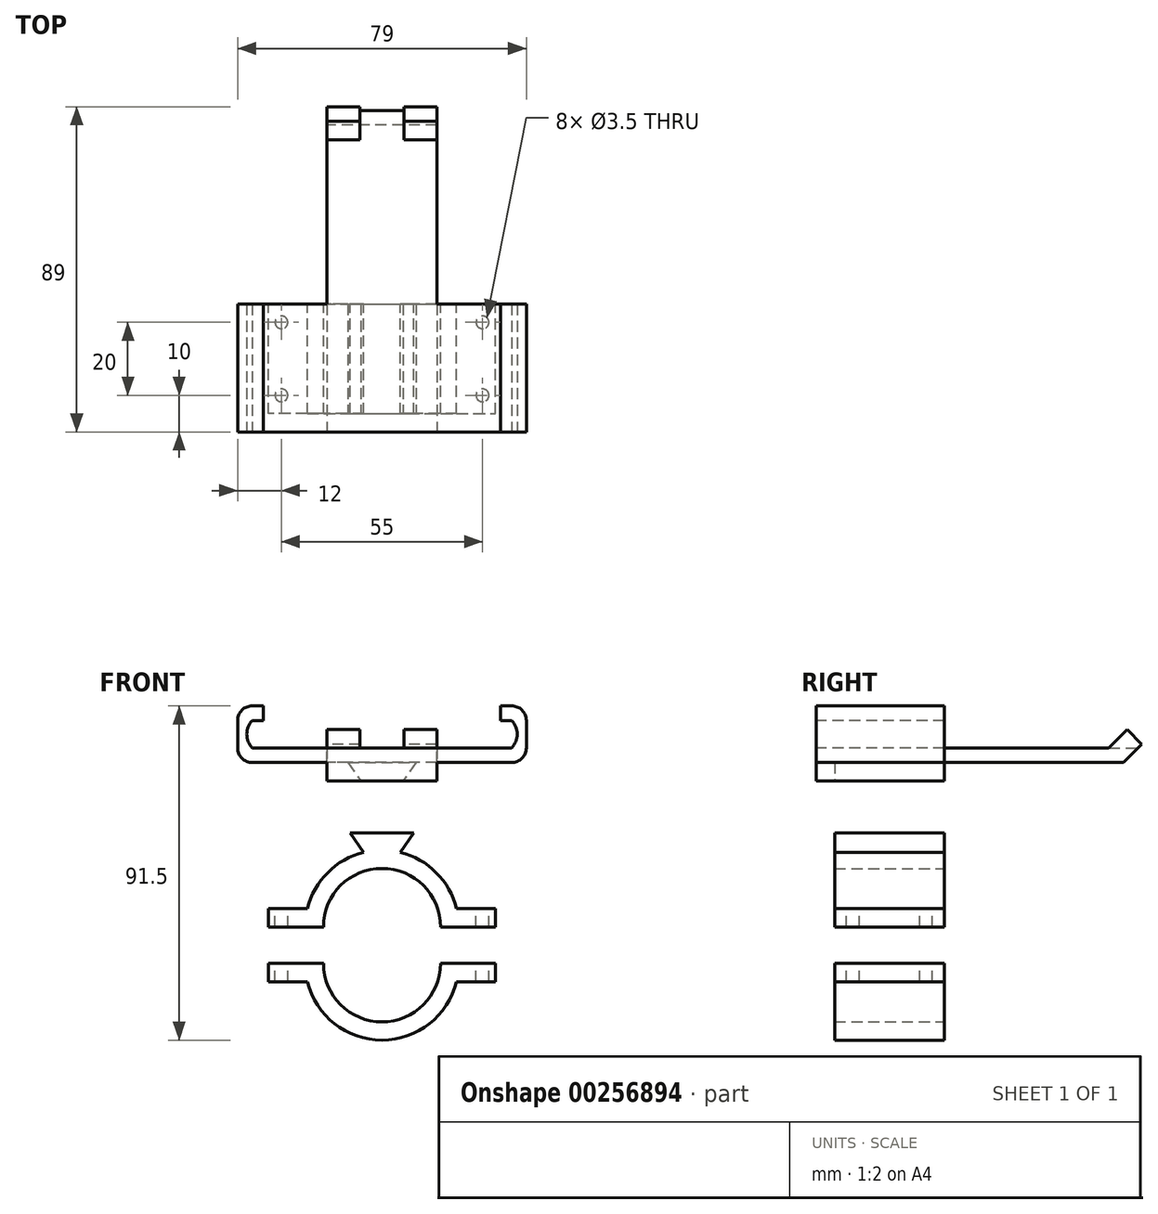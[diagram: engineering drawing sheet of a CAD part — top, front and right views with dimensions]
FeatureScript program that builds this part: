
annotation { "Feature Type Name" : "Feature", "Feature Type Description" : "" }
export const myFeature = defineFeature(function(context is Context, id is Id, definition is map)
    precondition{}
    {
        {
            var Q0;
            Q0=qCreatedBy(makeId("Front.planeOp"),FACE);
            var sketch = newSketch(context, id + "F0", { "sketchPlane" : qUnion([Q0])});
            skArc(sketch, "E0", {"start": v(16, 0) * mm, "mid": v(0, 16) * mm, "end": v(-16, 0) * mm});
            skArc(sketch, "E1", {"start": v(21, 0) * mm, "mid": v(0, 21) * mm, "end": v(-21, 0) * mm});
            skLineSegment(sketch, "E2", {"start": v(16, 0) * mm, "end": v(-16, 0) * mm, "construction": true});
            skLineSegment(sketch, "E3", {"start": v(21, 0) * mm, "end": v(16, 0) * mm});
            skLineSegment(sketch, "E4", {"start": v(-16, 0) * mm, "end": v(-21, 0) * mm});
            skLineSegment(sketch, "E5.bottom", {"start": v(16, 0) * mm, "end": v(31, 0) * mm});
            skLineSegment(sketch, "E5.top", {"start": v(16, 5) * mm, "end": v(31, 5) * mm});
            skLineSegment(sketch, "E5.left", {"start": v(16, 0) * mm, "end": v(16, 5) * mm});
            skLineSegment(sketch, "E5.right", {"start": v(31, 0) * mm, "end": v(31, 5) * mm});
            skLineSegment(sketch, "E6.bottom", {"start": v(-16, 0) * mm, "end": v(-31, 0) * mm});
            skLineSegment(sketch, "E6.top", {"start": v(-16, 5) * mm, "end": v(-31, 5) * mm});
            skLineSegment(sketch, "E6.left", {"start": v(-16, 0) * mm, "end": v(-16, 5) * mm});
            skLineSegment(sketch, "E6.right", {"start": v(-31, 0) * mm, "end": v(-31, 5) * mm});
            skLineSegment(sketch, "E7", {"start": v(-16, -10) * mm, "end": v(16, -10) * mm, "construction": true});
            skArc(sketch, "E8", {"start": v(-16, -10) * mm, "mid": v(0, -26) * mm, "end": v(16, -10) * mm});
            skLineSegment(sketch, "E9", {"start": v(16, -10) * mm, "end": v(21, -10) * mm});
            skLineSegment(sketch, "E10", {"start": v(-16, -10) * mm, "end": v(-21, -10) * mm});
            skArc(sketch, "E11", {"start": v(-21, -10) * mm, "mid": v(0, -31) * mm, "end": v(21, -10) * mm});
            skLineSegment(sketch, "E12.bottom", {"start": v(16, -10) * mm, "end": v(31, -10) * mm});
            skLineSegment(sketch, "E12.top", {"start": v(16, -15) * mm, "end": v(31, -15) * mm});
            skLineSegment(sketch, "E12.left", {"start": v(16, -10) * mm, "end": v(16, -15) * mm});
            skLineSegment(sketch, "E12.right", {"start": v(31, -10) * mm, "end": v(31, -15) * mm});
            skPoint(sketch, "E13.oppositeSnap0", {"position": v(23.5, -15) * mm});
            skLineSegment(sketch, "E13.bottom", {"start": v(-16, -10) * mm, "end": v(-31, -10) * mm});
            skLineSegment(sketch, "E13.top", {"start": v(-16, -15) * mm, "end": v(-31, -15) * mm});
            skLineSegment(sketch, "E13.left", {"start": v(-16, -10) * mm, "end": v(-16, -15) * mm});
            skLineSegment(sketch, "E13.right", {"start": v(-31, -10) * mm, "end": v(-31, -15) * mm});
            skPoint(sketch, "E14", {"position": v(0, 20.4) * mm});
            skLineSegment(sketch, "E15", {"start": v(-5, 20.4) * mm, "end": v(5, 20.4) * mm, "construction": true});
            skLineSegment(sketch, "E16", {"start": v(-5, 20.4) * mm, "end": v(-8.75, 25.75) * mm});
            skLineSegment(sketch, "E17", {"start": v(-8.75, 25.75) * mm, "end": v(8.75, 25.75) * mm});
            skLineSegment(sketch, "E18", {"start": v(8.75, 25.75) * mm, "end": v(5, 20.4) * mm});
            skPoint(sketch, "E19.endSnap0", {"position": v(0, 16) * mm});
            skSolve(sketch);
        }
        {
            var Q0;
            Q0=qCreatedBy(makeId("Front.planeOp"),FACE);
            cPlane(context, id + "F1", {"entities" : qUnion([Q0]), "cplaneType" : CPlaneType.OFFSET, "offset" : 30 * mm, "width" : 150 * mm, "height" : 150 * mm});
        }
        {
            var Q0;
            Q0=qCreatedBy(id+"F1.planeOp",FACE);
            var sketch = newSketch(context, id + "F2", { "sketchPlane" : qUnion([Q0])});
            skLineSegment(sketch, "E20", {"start": v(-35.5, 49) * mm, "end": v(35.5, 49) * mm});
            skLineSegment(sketch, "E21", {"start": v(-35.5, 56.5) * mm, "end": v(35.5, 56.5) * mm, "construction": true});
            skLineSegment(sketch, "E22", {"start": v(0, 49) * mm, "end": v(0, 56.5) * mm, "construction": true});
            skLineSegment(sketch, "E23", {"start": v(-9.3, 45) * mm, "end": v(9.3, 45) * mm});
            skLineSegment(sketch, "E24", {"start": v(9.3, 45) * mm, "end": v(5.8, 40) * mm});
            skLineSegment(sketch, "E25", {"start": v(-9.3, 45) * mm, "end": v(-5.8, 40) * mm});
            skLineSegment(sketch, "E26", {"start": v(5.8, 40) * mm, "end": v(15, 40) * mm});
            skLineSegment(sketch, "E27", {"start": v(15, 40) * mm, "end": v(15, 45) * mm});
            skLineSegment(sketch, "E28", {"start": v(15, 45) * mm, "end": v(35.5, 45) * mm});
            skLineSegment(sketch, "E29", {"start": v(-5.8, 40) * mm, "end": v(-15, 40) * mm});
            skLineSegment(sketch, "E30", {"start": v(-15, 40) * mm, "end": v(-15, 45) * mm});
            skLineSegment(sketch, "E31", {"start": v(-15, 45) * mm, "end": v(-35.5, 45) * mm});
            skArc(sketch, "E32", {"start": v(39.5, 56.5) * mm, "mid": v(38.33, 59.33) * mm, "end": v(35.5, 60.5) * mm});
            skArc(sketch, "E33", {"start": v(-35.5, 60.5) * mm, "mid": v(-38.33, 59.33) * mm, "end": v(-39.5, 56.5) * mm});
            skPoint(sketch, "E34", {"position": v(0, 45) * mm});
            skLineSegment(sketch, "E35", {"start": v(-5.8, 40) * mm, "end": v(5.8, 40) * mm});
            skLineSegment(sketch, "E36", {"start": v(0, 40) * mm, "end": v(0, 0) * mm, "construction": true});
            skLineSegment(sketch, "E37", {"start": v(39.5, 56.5) * mm, "end": v(39.5, 49) * mm});
            skArc(sketch, "E38", {"start": v(35.5, 45) * mm, "mid": v(38.33, 46.17) * mm, "end": v(39.5, 49) * mm});
            skLineSegment(sketch, "E39", {"start": v(-39.5, 56.5) * mm, "end": v(-39.5, 49) * mm});
            skArc(sketch, "E40", {"start": v(-35.5, 45) * mm, "mid": v(-38.33, 46.17) * mm, "end": v(-39.5, 49) * mm});
            skLineSegment(sketch, "E41", {"start": v(-35.5, 60.5) * mm, "end": v(-32.5, 60.5) * mm});
            skLineSegment(sketch, "E42", {"start": v(-32.5, 60.5) * mm, "end": v(-32.5, 56.5) * mm});
            skLineSegment(sketch, "E43", {"start": v(-32.5, 56.5) * mm, "end": v(-35.5, 56.5) * mm});
            skLineSegment(sketch, "E44", {"start": v(35.5, 60.5) * mm, "end": v(32.5, 60.5) * mm});
            skLineSegment(sketch, "E45", {"start": v(32.5, 60.5) * mm, "end": v(32.5, 56.5) * mm});
            skLineSegment(sketch, "E46", {"start": v(32.5, 56.5) * mm, "end": v(35.5, 56.5) * mm});
            skArc(sketch, "E47", {"start": v(35.5, 49) * mm, "mid": v(36.98, 52.75) * mm, "end": v(35.5, 56.5) * mm});
            skArc(sketch, "E48", {"start": v(-35.5, 56.5) * mm, "mid": v(-36.98, 52.75) * mm, "end": v(-35.5, 49) * mm});
            skSolve(sketch);
        }
        {
            var Q0;
            Q0=makeQuery(id+"F0.imprint","IMPRINT",FACE,{"disambiguationData":[TD([[makeQuery(id+"F0.imprint","IMPRINT",EDGE,{"derivedFrom":sQuery(id+"F0.wireOp",EDGE,"mbzJrH7V-MKxJ-bzjF-v4ra-i13s79XAPloW")}),-1.0]])]});
            var Q1;
            Q1=makeQuery(id+"F2.imprint","IMPRINT",FACE,{"disambiguationData":[TD([[makeQuery(id+"F2.imprint","IMPRINT",EDGE,{"derivedFrom":sQuery(id+"F2.wireOp",EDGE,"E20")}),-1.0]])]});
            extrude(context, id + "F3", {"entities" : qUnion([Q0, Q1]), "oppositeDirection" : true, "depth" : 30 * mm});
        }
        {
            var Q0;
            Q0=makeQuery(id+"F2.imprint","IMPRINT",FACE,{"disambiguationData":[TD([[makeQuery(id+"F2.imprint","IMPRINT",EDGE,{"derivedFrom":sQuery(id+"F2.wireOp",EDGE,"E20")}),-1.0]])]});
            var Q1;
            Q1=makeQuery(id+"F2.imprint","IMPRINT",FACE,{"disambiguationData":[TD([[makeQuery(id+"F2.imprint","IMPRINT",EDGE,{"derivedFrom":sQuery(id+"F2.wireOp",EDGE,"E23")}),-1.0]])]});
            extrude(context, id + "F4", {"entities" : qUnion([Q0, Q1]), "operationType" : NewBodyOperationType.ADD, "depth" : 5 * mm});
        }
        {
            var Q0;
            Q0=qCreatedBy(makeId("Right.planeOp"),FACE);
            var sketch = newSketch(context, id + "F5", { "sketchPlane" : qUnion([Q0])});
            skLineSegment(sketch, "E49.left", {"start": v(0, 49) * mm, "end": v(0, 45) * mm});
            skLineSegment(sketch, "E50", {"start": v(0, 49) * mm, "end": v(45, 49) * mm});
            skLineSegment(sketch, "E51", {"start": v(45, 49) * mm, "end": v(50, 54) * mm});
            skLineSegment(sketch, "E52", {"start": v(45, 49) * mm, "end": v(49, 45) * mm, "construction": true});
            skLineSegment(sketch, "E53", {"start": v(0, 45) * mm, "end": v(49, 45) * mm});
            skLineSegment(sketch, "E54", {"start": v(49, 45) * mm, "end": v(54, 50) * mm});
            skLineSegment(sketch, "E55", {"start": v(54, 50) * mm, "end": v(50, 54) * mm});
            skLineSegment(sketch, "E56", {"start": v(45, 49) * mm, "end": v(53, 49) * mm});
            skSolve(sketch);
        }
        {
            var Q0;
            Q0=qSketchRegion(id+"F5",true);
            extrude(context, id + "F6", {"entities" : qUnion([Q0]), "operationType" : NewBodyOperationType.ADD, "depth" : 15 * mm, "hasSecondDirection" : true, "secondDirectionOppositeDirection" : true, "secondDirectionDepth" : 15 * mm});
        }
        {
            var Q0;
            Q0=makeQuery(id+"F5.imprint","IMPRINT",FACE,{"disambiguationData":[TD([[makeQuery(id+"F5.imprint","IMPRINT",EDGE,{"derivedFrom":sQuery(id+"F5.wireOp",EDGE,"E51")}),-1.0]])]});
            extrude(context, id + "F7", {"entities" : qUnion([Q0]), "operationType" : NewBodyOperationType.REMOVE, "endBound" : BoundingType.SYMMETRIC, "oppositeDirection" : true, "depth" : 12 * mm, "hasSecondDirection" : true, "secondDirectionOppositeDirection" : true, "secondDirectionDepth" : 6 * mm});
        }
        {
            var Q0;
            {var subQ5=sQuery(id+"F0.wireOp",EDGE,"E6.right");Q0=makeQuery(id+"F0.imprint","IMPRINT",FACE,{"disambiguationData":[TD([[makeQuery(id+"F0.imprint","IMPRINT",EDGE,{"derivedFrom":subQ5}),-1.0]])]});}
            var Q1;
            {var subQ5=sQuery(id+"F0.wireOp",EDGE,"E6.left");Q1=makeQuery(id+"F0.imprint","IMPRINT",FACE,{"disambiguationData":[TD([[makeQuery(id+"F0.imprint","IMPRINT",EDGE,{"derivedFrom":subQ5}),1.0]])]});}
            var Q2;
            Q2=makeQuery(id+"F0.imprint","IMPRINT",FACE,{"disambiguationData":[TD([[makeQuery(id+"F0.imprint","IMPRINT",EDGE,{"derivedFrom":sQuery(id+"F0.wireOp",EDGE,"E0")}),-1.0]])]});
            var Q3;
            {var subQ5=sQuery(id+"F0.wireOp",EDGE,"E5.left");Q3=makeQuery(id+"F0.imprint","IMPRINT",FACE,{"disambiguationData":[TD([[makeQuery(id+"F0.imprint","IMPRINT",EDGE,{"derivedFrom":subQ5}),-1.0]])]});}
            var Q4;
            {var subQ5=sQuery(id+"F0.wireOp",EDGE,"E5.right");Q4=makeQuery(id+"F0.imprint","IMPRINT",FACE,{"disambiguationData":[TD([[makeQuery(id+"F0.imprint","IMPRINT",EDGE,{"derivedFrom":subQ5}),1.0]])]});}
            var Q5;
            {var subQ0=sQuery(id+"F0.wireOp",EDGE,"E16");Q5=makeQuery(id+"F0.imprint","IMPRINT",FACE,{"disambiguationData":[TD([[makeQuery(id+"F0.imprint","IMPRINT",EDGE,{"derivedFrom":subQ0}),-1.0]])]});}
            extrude(context, id + "F8", {"entities" : qUnion([Q0, Q1, Q2, Q3, Q4, Q5]), "depth" : 30 * mm});
        }
        {
            var Q0;
            {var subQ5=sQuery(id+"F0.wireOp",EDGE,"E13.right");Q0=makeQuery(id+"F0.imprint","IMPRINT",FACE,{"disambiguationData":[TD([[makeQuery(id+"F0.imprint","IMPRINT",EDGE,{"derivedFrom":subQ5}),1.0]])]});}
            var Q1;
            {var subQ5=sQuery(id+"F0.wireOp",EDGE,"E13.left");Q1=makeQuery(id+"F0.imprint","IMPRINT",FACE,{"disambiguationData":[TD([[makeQuery(id+"F0.imprint","IMPRINT",EDGE,{"derivedFrom":subQ5}),-1.0]])]});}
            var Q2;
            Q2=makeQuery(id+"F0.imprint","IMPRINT",FACE,{"disambiguationData":[TD([[makeQuery(id+"F0.imprint","IMPRINT",EDGE,{"derivedFrom":sQuery(id+"F0.wireOp",EDGE,"E8")}),-1.0]])]});
            var Q3;
            {var subQ5=sQuery(id+"F0.wireOp",EDGE,"E12.left");Q3=makeQuery(id+"F0.imprint","IMPRINT",FACE,{"disambiguationData":[TD([[makeQuery(id+"F0.imprint","IMPRINT",EDGE,{"derivedFrom":subQ5}),1.0]])]});}
            var Q4;
            {var subQ5=sQuery(id+"F0.wireOp",EDGE,"E12.right");Q4=makeQuery(id+"F0.imprint","IMPRINT",FACE,{"disambiguationData":[TD([[makeQuery(id+"F0.imprint","IMPRINT",EDGE,{"derivedFrom":subQ5}),-1.0]])]});}
            extrude(context, id + "F9", {"entities" : qUnion([Q0, Q1, Q2, Q3, Q4]), "depth" : 30 * mm});
        }
        {
            var Q0;
            Q0=makeQuery(id+"F8.opExtrude","SWEPT_FACE",FACE,{"disambiguationData":[OSD([sQuery(id+"F0.wireOp",EDGE,"E6.top")])]});
            var sketch = newSketch(context, id + "F10", { "sketchPlane" : qUnion([Q0])});
            skCircle(sketch, "E57", {"center": v(-27.5, -25) * mm, "radius": 1.75 * mm});
            skCircle(sketch, "E58", {"center": v(-27.5, -5) * mm, "radius": 1.75 * mm});
            skCircle(sketch, "E59", {"center": v(27.5, -5) * mm, "radius": 1.75 * mm});
            skCircle(sketch, "E60", {"center": v(27.5, -25) * mm, "radius": 1.75 * mm});
            skLineSegment(sketch, "E61", {"start": v(27.5, -15) * mm, "end": v(-27.5, -15) * mm, "construction": true});
            skLineSegment(sketch, "E62", {"start": v(-27.5, -5) * mm, "end": v(-27.5, -25) * mm, "construction": true});
            skLineSegment(sketch, "E63", {"start": v(27.5, -5) * mm, "end": v(27.5, -25) * mm, "construction": true});
            skLineSegment(sketch, "E64", {"start": v(0, 0) * mm, "end": v(0, -15) * mm, "construction": true});
            skSolve(sketch);
        }
        {
            var Q0;
            Q0=qSketchRegion(id+"F10",true);
            extrude(context, id + "F11", {"entities" : qUnion([Q0]), "operationType" : NewBodyOperationType.REMOVE, "oppositeDirection" : true, "depth" : 50 * mm});
        }
    });
